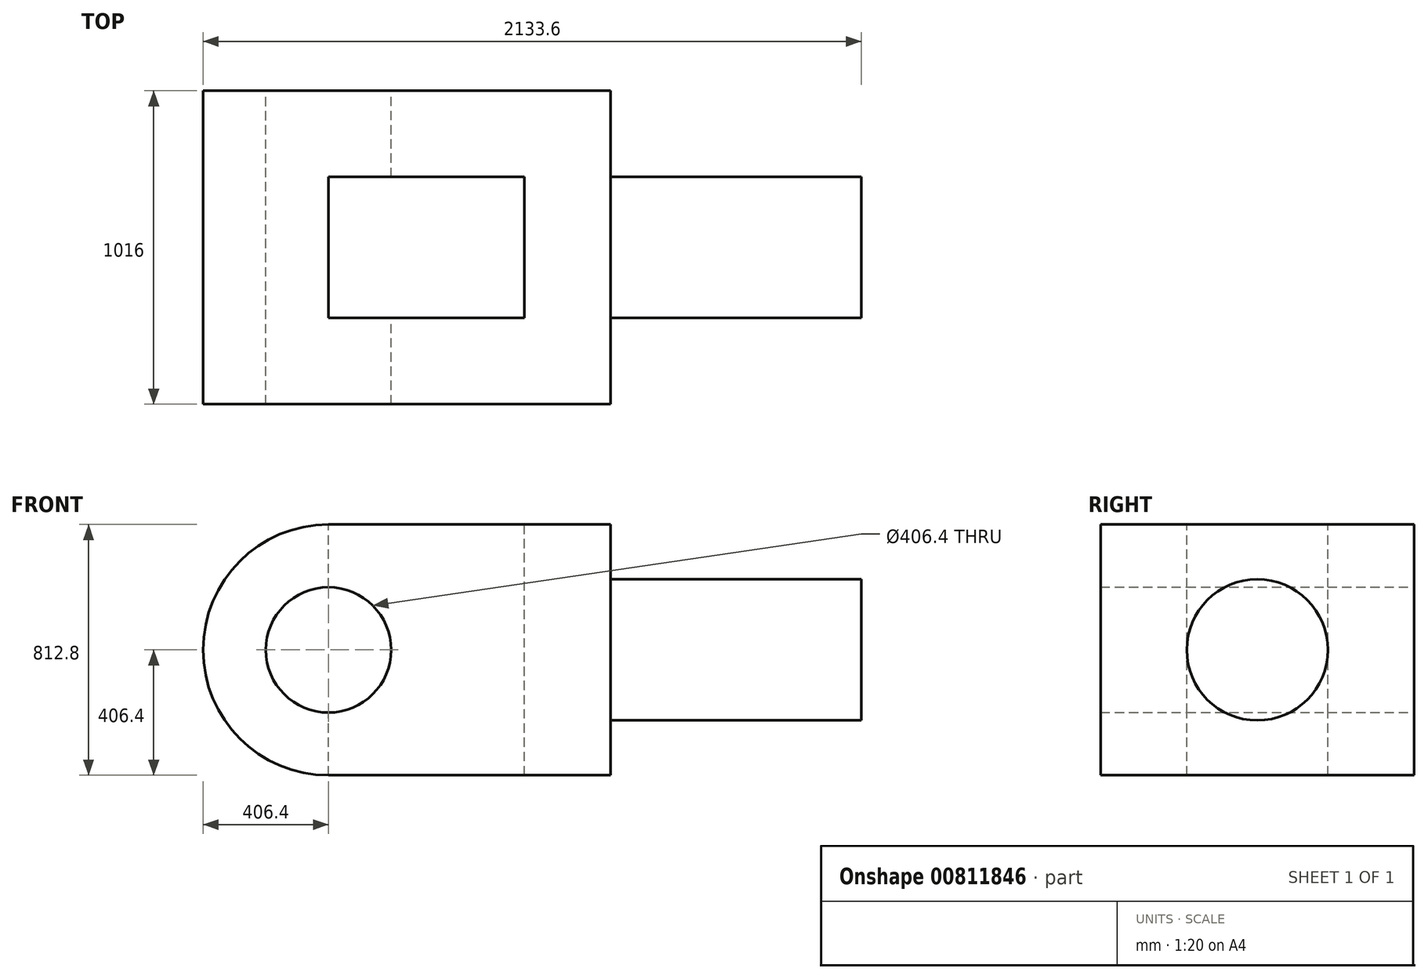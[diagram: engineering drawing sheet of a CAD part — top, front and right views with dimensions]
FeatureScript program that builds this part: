
annotation { "Feature Type Name" : "Feature", "Feature Type Description" : "" }
export const myFeature = defineFeature(function(context is Context, id is Id, definition is map)
    precondition{}
    {
        {
            var Q0;
            Q0=qCreatedBy(makeId("Front.planeOp"),FACE);
            var sketch = newSketch(context, id + "F0", { "sketchPlane" : qUnion([Q0])});
            skCircle(sketch, "E0", {"center": v(0, 0) * mm, "radius": 203.2 * mm});
            skCircle(sketch, "E1", {"center": v(0, 0) * mm, "radius": 406.4 * mm});
            skLineSegment(sketch, "E2", {"start": v(0, 406.4) * mm, "end": v(914.4, 406.4) * mm});
            skLineSegment(sketch, "E3", {"start": v(0, -406.4) * mm, "end": v(914.4, -406.4) * mm});
            skLineSegment(sketch, "E4", {"start": v(914.4, -406.4) * mm, "end": v(914.4, 406.4) * mm});
            skPoint(sketch, "E5.endSnap0", {"position": v(914.4, 0) * mm});
            skLineSegment(sketch, "E6", {"start": v(1727.2, 0) * mm, "end": v(1727.2, 228.6) * mm});
            skLineSegment(sketch, "E7", {"start": v(1727.2, 228.6) * mm, "end": v(1727.2, -228.6) * mm});
            skPoint(sketch, "E7.endSnap0", {"position": v(1727.2, 114.3) * mm});
            skLineSegment(sketch, "E8", {"start": v(1727.2, 228.6) * mm, "end": v(914.4, 228.6) * mm});
            skLineSegment(sketch, "E9", {"start": v(1727.2, -228.6) * mm, "end": v(914.4, -228.6) * mm});
            skSolve(sketch);
        }
        {
            var Q0;
            Q0=makeQuery(id+"F0.imprint","IMPRINT",FACE,{"disambiguationData":[TD([[makeQuery(id+"F0.imprint","IMPRINT",EDGE,{"derivedFrom":sQuery(id+"F0.wireOp",EDGE,"E0")}),-1.0]])]});
            var Q1;
            {var subQ3=sQuery(id+"F0.wireOp",EDGE,"E2");Q1=makeQuery(id+"F0.imprint","IMPRINT",FACE,{"disambiguationData":[TD([[makeQuery(id+"F0.imprint","IMPRINT",EDGE,{"derivedFrom":subQ3}),-1.0]])]});}
            extrude(context, id + "F1", {"entities" : qUnion([Q0, Q1]), "depth" : 508 * mm, "offsetDistance" : 25.4 * mm});
        }
        {
            var Q0;
            Q0=makeQuery(id+"F0.imprint","IMPRINT",FACE,{"disambiguationData":[TD([[makeQuery(id+"F0.imprint","IMPRINT",EDGE,{"derivedFrom":sQuery(id+"F0.wireOp",EDGE,"E0")}),-1.0]])]});
            var Q1;
            {var subQ3=sQuery(id+"F0.wireOp",EDGE,"E2");Q1=makeQuery(id+"F0.imprint","IMPRINT",FACE,{"disambiguationData":[TD([[makeQuery(id+"F0.imprint","IMPRINT",EDGE,{"derivedFrom":subQ3}),-1.0]])]});}
            extrude(context, id + "F2", {"entities" : qUnion([Q0, Q1]), "operationType" : NewBodyOperationType.ADD, "oppositeDirection" : true, "depth" : 508 * mm, "offsetDistance" : 25.4 * mm});
        }
        {
            var Q0;
            {var subQ0=sQuery(id+"F0.wireOp",EDGE,"E4");Q0=makeQuery(id+"F2.boolean.opBoolean","MERGE",FACE,{"derivedFrom":[makeQuery(id+"F1.opExtrude","SWEPT_FACE",FACE,{"disambiguationData":[OSD([subQ0])]}),makeQuery(id+"F2.opExtrude","SWEPT_FACE",FACE,{"disambiguationData":[OSD([subQ0])]})]});}
            var sketch = newSketch(context, id + "F3", { "sketchPlane" : qUnion([Q0])});
            skCircle(sketch, "E10", {"center": v(0, 0) * mm, "radius": 228.6 * mm});
            skSolve(sketch);
        }
        {
            var Q0;
            Q0=qSketchRegion(id+"F3",true);
            extrude(context, id + "F4", {"entities" : qUnion([Q0]), "operationType" : NewBodyOperationType.ADD, "depth" : 812.8 * mm, "offsetDistance" : 25.4 * mm});
        }
        {
            var Q0;
            {var subQ0=sQuery(id+"F0.wireOp",EDGE,"E2");Q0=makeQuery(id+"F2.boolean.opBoolean","MERGE",FACE,{"derivedFrom":[makeQuery(id+"F1.opExtrude","SWEPT_FACE",FACE,{"disambiguationData":[OSD([subQ0])]}),makeQuery(id+"F2.opExtrude","SWEPT_FACE",FACE,{"disambiguationData":[OSD([subQ0])]})]});}
            var sketch = newSketch(context, id + "F5", { "sketchPlane" : qUnion([Q0])});
            skLineSegment(sketch, "E11.bottom", {"start": v(914.4, 508) * mm, "end": v(-406.4, 508) * mm});
            skLineSegment(sketch, "E11.top", {"start": v(914.4, -508) * mm, "end": v(-406.4, -508) * mm});
            skLineSegment(sketch, "E11.left", {"start": v(914.4, 508) * mm, "end": v(914.4, -508) * mm});
            skLineSegment(sketch, "E11.right", {"start": v(-406.4, 508) * mm, "end": v(-406.4, -508) * mm});
            skLineSegment(sketch, "E12", {"start": v(-406.4, 508) * mm, "end": v(-406.4, 228.6) * mm});
            skLineSegment(sketch, "E13.bottom", {"start": v(-406.4, 228.6) * mm, "end": v(635, 228.6) * mm});
            skLineSegment(sketch, "E13.top", {"start": v(-406.4, -228.6) * mm, "end": v(635, -228.6) * mm});
            skLineSegment(sketch, "E13.left", {"start": v(-406.4, 228.6) * mm, "end": v(-406.4, -228.6) * mm});
            skLineSegment(sketch, "E13.right", {"start": v(635, 228.6) * mm, "end": v(635, -228.6) * mm});
            skSolve(sketch);
        }
        {
            var Q0;
            {var subQ0=sQuery(id+"F5.wireOp",EDGE,"E13.right");Q0=makeQuery(id+"F5.imprint","IMPRINT",FACE,{"disambiguationData":[TD([[makeQuery(id+"F5.imprint","IMPRINT",EDGE,{"derivedFrom":subQ0}),-1.0]])]});}
            var Q1;
            {var subQ0=sQuery(id+"F5.wireOp",EDGE,"E13.left");Q1=makeQuery(id+"F5.imprint","IMPRINT",FACE,{"disambiguationData":[TD([[makeQuery(id+"F5.imprint","IMPRINT",EDGE,{"derivedFrom":subQ0}),1.0]])]});}
            extrude(context, id + "F6", {"entities" : qUnion([Q0, Q1]), "operationType" : NewBodyOperationType.REMOVE, "endBound" : BoundingType.THROUGH_ALL, "oppositeDirection" : true, "depth" : 25.4 * mm, "offsetDistance" : 25.4 * mm});
        }
    });
